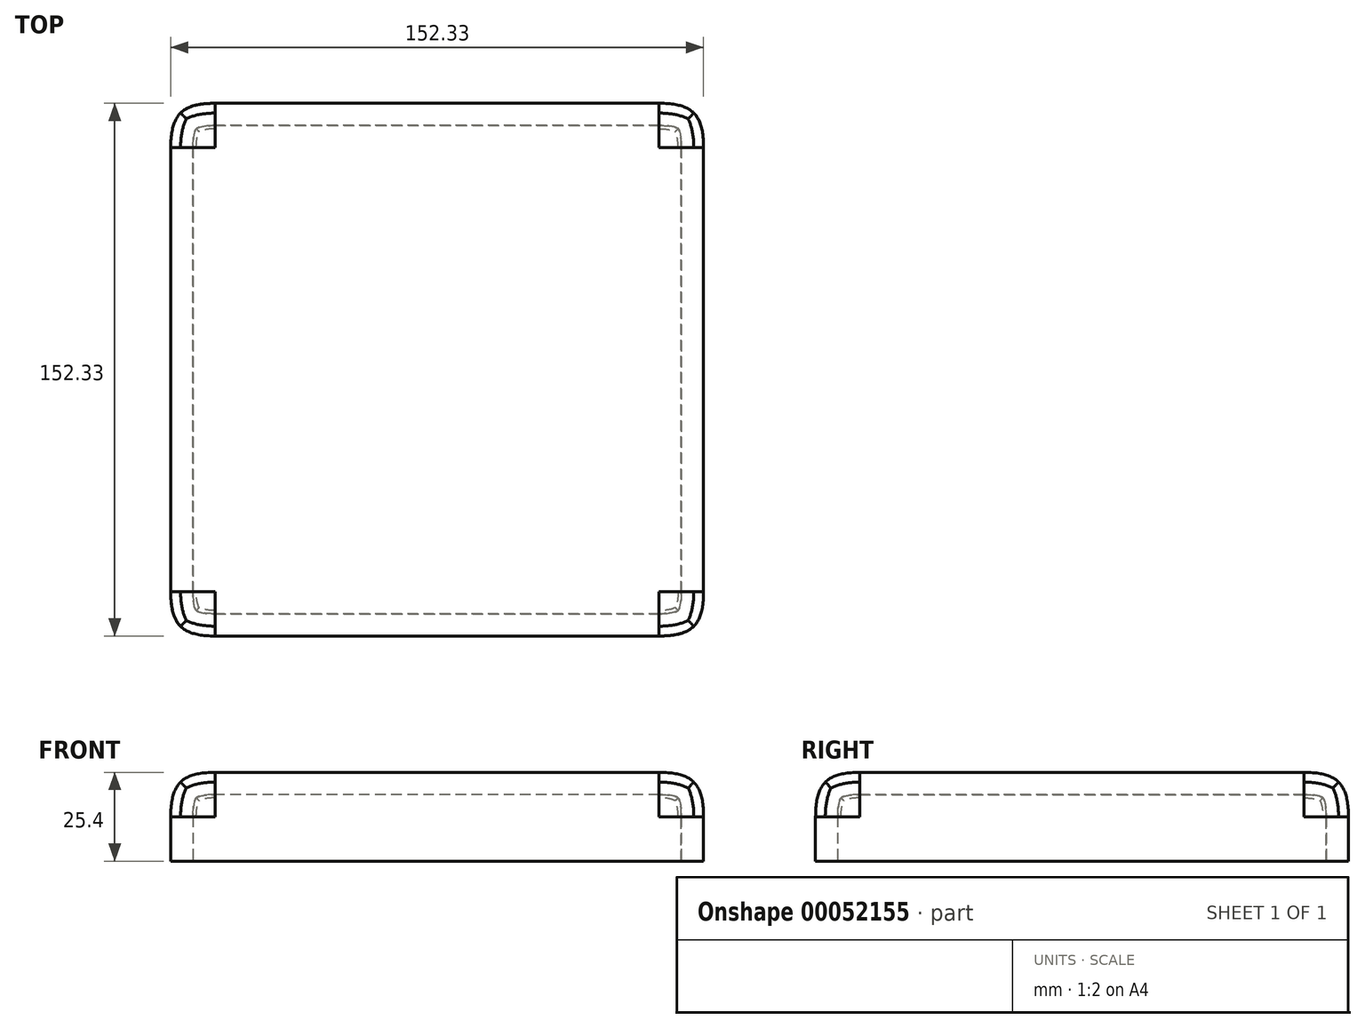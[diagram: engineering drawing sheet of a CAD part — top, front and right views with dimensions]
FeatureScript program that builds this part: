
annotation { "Feature Type Name" : "Feature", "Feature Type Description" : "" }
export const myFeature = defineFeature(function(context is Context, id is Id, definition is map)
    precondition{}
    {
        {
            var Q0;
            Q0=qCreatedBy(makeId("Top.planeOp"),FACE);
            var sketch = newSketch(context, id + "F0", { "sketchPlane" : qUnion([Q0])});
            skLineSegment(sketch, "E0.bottom", {"start": v(-76.66, 76.41) * mm, "end": v(75.67, 76.41) * mm});
            skLineSegment(sketch, "E0.top", {"start": v(-76.66, -75.92) * mm, "end": v(75.67, -75.92) * mm});
            skLineSegment(sketch, "E0.left", {"start": v(-76.66, 76.41) * mm, "end": v(-76.66, -75.92) * mm});
            skLineSegment(sketch, "E0.right", {"start": v(75.67, 76.41) * mm, "end": v(75.67, -75.92) * mm});
            skSolve(sketch);
        }
        {
            var Q0;
            Q0=makeQuery(id+"F0.imprint","IMPRINT",FACE,{"disambiguationData":[TD([[makeQuery(id+"F0.imprint","IMPRINT",EDGE,{"derivedFrom":sQuery(id+"F0.wireOp",EDGE,"E0.bottom")}),-1.0]])]});
            extrude(context, id + "F1", {"entities" : qUnion([Q0]), "depth" : 25.4 * mm});
        }
        {
            var Q0;
            Q0=makeQuery(id+"F1.opExtrude","CAP_EDGE",EDGE,{"disambiguationData":[OSD([sQuery(id+"F0.wireOp",EDGE,"E0.top")])],"isStart":false});
            var Q1;
            Q1=makeQuery(id+"F1.opExtrude","SWEPT_EDGE",EDGE,{"disambiguationData":[OSD([sQuery(id+"F0.wireOp",EDGE,"E0.top"),sQuery(id+"F0.wireOp",EDGE,"E0.left")])]});
            var Q2;
            Q2=makeQuery(id+"F1.opExtrude","SWEPT_EDGE",EDGE,{"disambiguationData":[OSD([sQuery(id+"F0.wireOp",EDGE,"E0.top"),sQuery(id+"F0.wireOp",EDGE,"E0.right")])]});
            var Q3;
            Q3=makeQuery(id+"F1.opExtrude","CAP_EDGE",EDGE,{"disambiguationData":[OSD([sQuery(id+"F0.wireOp",EDGE,"E0.right")])],"isStart":false});
            var Q4;
            Q4=makeQuery(id+"F1.opExtrude","CAP_EDGE",EDGE,{"disambiguationData":[OSD([sQuery(id+"F0.wireOp",EDGE,"E0.bottom")])],"isStart":false});
            var Q5;
            Q5=makeQuery(id+"F1.opExtrude","SWEPT_EDGE",EDGE,{"disambiguationData":[OSD([sQuery(id+"F0.wireOp",EDGE,"E0.bottom"),sQuery(id+"F0.wireOp",EDGE,"E0.right")])]});
            var Q6;
            Q6=makeQuery(id+"F1.opExtrude","SWEPT_EDGE",EDGE,{"disambiguationData":[OSD([sQuery(id+"F0.wireOp",EDGE,"E0.bottom"),sQuery(id+"F0.wireOp",EDGE,"E0.left")])]});
            var Q7;
            Q7=makeQuery(id+"F1.opExtrude","CAP_EDGE",EDGE,{"disambiguationData":[OSD([sQuery(id+"F0.wireOp",EDGE,"E0.left")])],"isStart":false});
            fillet(context, id + "F2", {"entities" : qUnion([Q0, Q1, Q2, Q3, Q4, Q5, Q6, Q7]), "radius" : 12.7 * mm, "tangentPropagation" : true, "rho" : 0.56, "crossSection" : FilletCrossSection.CONIC, "allowEdgeOverflow" : false});
        }
        {
            var Q0;
            Q0=makeQuery(id+"F1.opExtrude","CAP_FACE",FACE,{"disambiguationData":[OSD([sQuery(id+"F0.wireOp",EDGE,"E0.bottom"),sQuery(id+"F0.wireOp",EDGE,"E0.top"),sQuery(id+"F0.wireOp",EDGE,"E0.left"),sQuery(id+"F0.wireOp",EDGE,"E0.right")])],"isStart":true});
            shell(context, id + "F3", {"entities" : qUnion([Q0]), "thickness" : 6.35 * mm});
        }
    });
